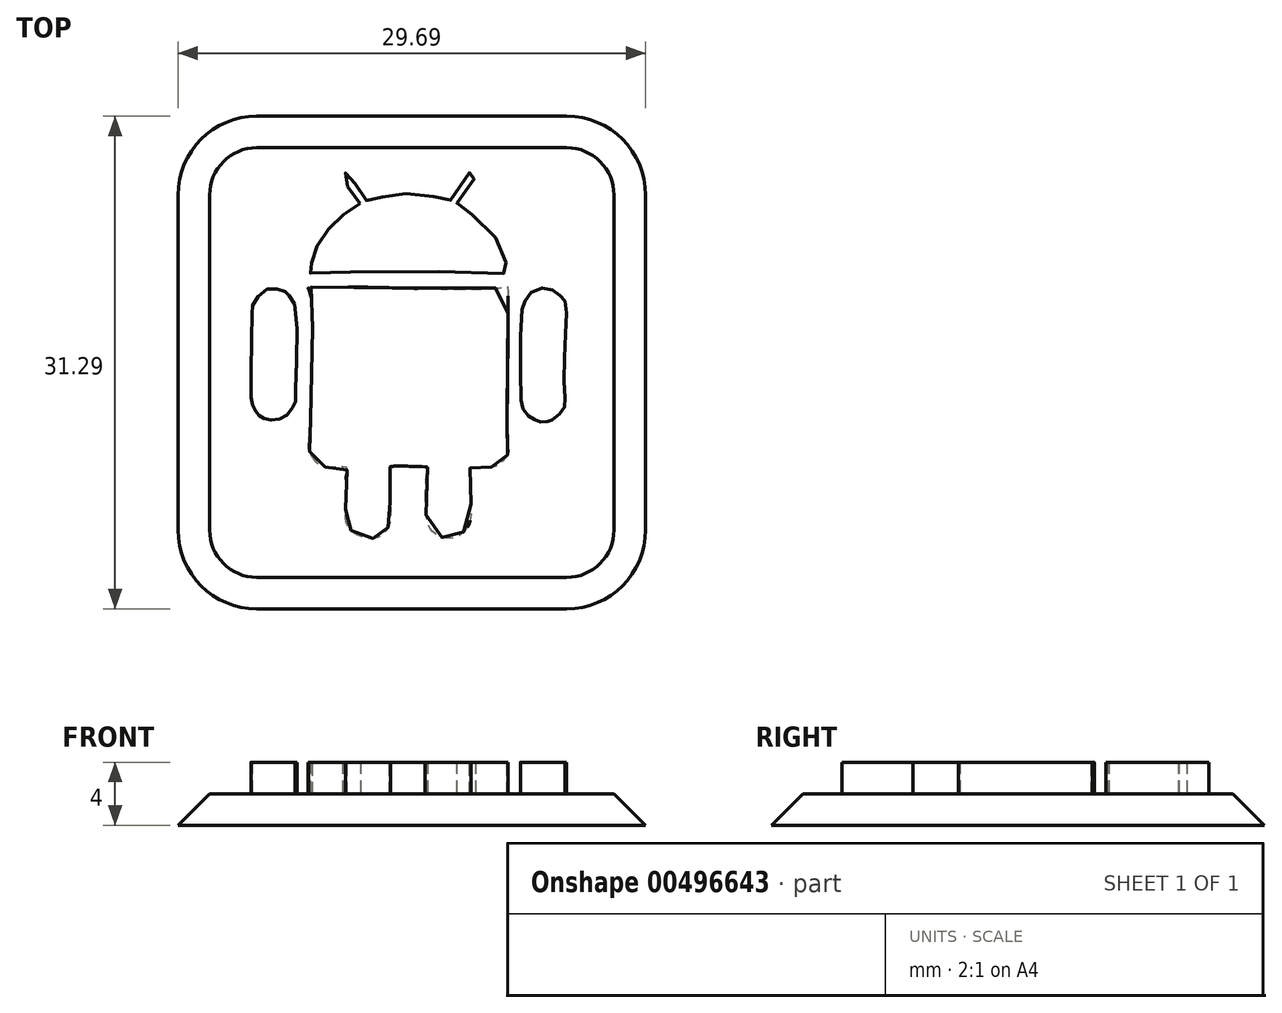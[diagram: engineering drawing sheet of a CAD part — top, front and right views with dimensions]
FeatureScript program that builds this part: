
annotation { "Feature Type Name" : "Feature", "Feature Type Description" : "" }
export const myFeature = defineFeature(function(context is Context, id is Id, definition is map)
    precondition{}
    {
        {
            var Q0;
            Q0=qCreatedBy(makeId("Top.planeOp"),FACE);
            var sketch = newSketch(context, id + "F0", { "sketchPlane" : qUnion([Q0])});
            skFitSpline(sketch, "E0", {"points": [v(6.96, 9.56) * mm, v(7.27, 9.15) * mm, v(7.6, 8.92) * mm, v(7.9, 8.8) * mm, v(8.1, 8.73) * mm, v(8.47, 8.77) * mm, v(8.65, 8.8) * mm, v(8.83, 8.9) * mm, v(9.36, 9.35) * mm, v(9.61, 9.73) * mm, v(9.59, 10.46) * mm, v(9.61, 13.76) * mm, v(9.65, 16.27) * mm, v(9.46, 16.6) * mm, v(9.1, 16.94) * mm, v(8.48, 17.25) * mm, v(7.55, 17.03) * mm, v(7.06, 16.44) * mm, v(6.88, 15.86) * mm, v(6.85, 9.87) * mm, v(6.96, 9.56) * mm]});
            skFitSpline(sketch, "E1", {"points": [v(-10.23, 9.83) * mm, v(-10.07, 9.46) * mm, v(-9.88, 9.2) * mm, v(-9.64, 9.02) * mm, v(-9.38, 8.9) * mm, v(-8.85, 8.85) * mm, v(-8.25, 9.02) * mm, v(-7.78, 9.48) * mm, v(-7.52, 10) * mm, v(-7.51, 10.18) * mm, v(-7.55, 16.14) * mm, v(-7.98, 16.83) * mm, v(-8.16, 17.03) * mm, v(-8.75, 17.2) * mm, v(-9.55, 17.05) * mm, v(-10.22, 16.15) * mm, v(-10.24, 15.87) * mm, v(-10.32, 10.12) * mm, v(-10.23, 9.83) * mm]});
            skFitSpline(sketch, "E2", {"points": [v(-3.39, 22.6) * mm, v(-4.18, 22.1) * mm, v(-5.1, 21.36) * mm, v(-5.7, 20.55) * mm, v(-6.3, 19.6) * mm, v(-6.48, 18.86) * mm, v(-6.55, 18.51) * mm, v(-6.58, 18.22) * mm, v(-6.17, 18.2) * mm, v(5.9, 18.15) * mm, v(6, 18.13) * mm, v(5.75, 19.3) * mm, v(4.78, 20.97) * mm, v(2.9, 22.45) * mm, v(2.73, 22.59) * mm, v(3.89, 24.25) * mm, v(3.89, 24.54) * mm, v(3.63, 24.64) * mm, v(2.3, 22.74) * mm, v(2.27, 22.73) * mm, v(0.73, 23.16) * mm, v(-0.9, 23.2) * mm, v(-2.35, 22.93) * mm, v(-2.93, 22.77) * mm, v(-3.16, 23.11) * mm, v(-3.97, 24.23) * mm, v(-4.23, 24.56) * mm, v(-4.43, 24.51) * mm, v(-4.51, 24.3) * mm, v(-3.48, 22.77) * mm, v(-3.39, 22.6) * mm]});
            skFitSpline(sketch, "E3", {"points": [v(-1.5, 5.85) * mm, v(-1.5, 3.85) * mm, v(-1.48, 2.52) * mm, v(-1.73, 1.87) * mm, v(-2.2, 1.44) * mm, v(-2.76, 1.34) * mm, v(-3.71, 1.63) * mm, v(-4.26, 2.33) * mm, v(-4.31, 3.04) * mm, v(-4.24, 5.64) * mm, v(-4.26, 5.87) * mm, v(-5.64, 5.87) * mm, v(-6.26, 6.27) * mm, v(-6.66, 7) * mm, v(-6.65, 7.58) * mm, v(-6.6, 16.96) * mm, v(-6.61, 17.28) * mm, v(5.71, 17.3) * mm, v(5.97, 17.3) * mm, v(5.98, 7.04) * mm, v(5.99, 6.69) * mm, v(5.56, 6.17) * mm, v(5.1, 5.9) * mm, v(3.87, 5.87) * mm, v(3.6, 5.83) * mm, v(3.57, 5.65) * mm, v(3.6, 2.58) * mm, v(3.24, 1.83) * mm, v(2.66, 1.4) * mm, v(1.6, 1.48) * mm, v(0.87, 2.4) * mm, v(0.88, 5.89) * mm], "startDerivative": vector(-1.38, -52.63) * mm, "endDerivative": vector(6.9, 77.46) * mm});
            skFitSpline(sketch, "E4", {"points": [v(0.88, 5.89) * mm, v(-1.5, 5.89) * mm, v(-1.5, 5.85) * mm], "startDerivative": vector(-3.87, 0.15) * mm, "endDerivative": vector(-0.1, -0.44) * mm});
            skLineSegment(sketch, "E5.bottom", {"start": v(-9.96, 28.16) * mm, "end": v(9.73, 28.16) * mm});
            skLineSegment(sketch, "E5.top", {"start": v(-9.96, -3.13) * mm, "end": v(9.73, -3.13) * mm});
            skLineSegment(sketch, "E5.left", {"start": v(-14.96, 23.16) * mm, "end": v(-14.96, 1.87) * mm});
            skLineSegment(sketch, "E5.right", {"start": v(14.73, 23.16) * mm, "end": v(14.73, 1.87) * mm});
            skPoint(sketch, "E6.visualSharp", {"position": v(-14.96, 28.16) * mm});
            skArc(sketch, "E6.filletArc", {"start": v(-9.96, 28.16) * mm, "mid": v(-13.5, 26.7) * mm, "end": v(-14.96, 23.16) * mm});
            skPoint(sketch, "E7.visualSharp", {"position": v(14.73, 28.16) * mm});
            skArc(sketch, "E7.filletArc", {"start": v(14.73, 23.16) * mm, "mid": v(13.26, 26.7) * mm, "end": v(9.73, 28.16) * mm});
            skPoint(sketch, "E8.visualSharp", {"position": v(14.73, -3.13) * mm});
            skArc(sketch, "E8.filletArc", {"start": v(9.73, -3.13) * mm, "mid": v(13.26, -1.67) * mm, "end": v(14.73, 1.87) * mm});
            skPoint(sketch, "E9.visualSharp", {"position": v(-14.96, -3.13) * mm});
            skArc(sketch, "E9.filletArc", {"start": v(-14.96, 1.87) * mm, "mid": v(-13.5, -1.67) * mm, "end": v(-9.96, -3.13) * mm});
            skSolve(sketch);
        }
        {
            var Q0;
            Q0 = qSketchRegion(id + "F0", true);
            extrude(context, id + "F1", {"entities" : qUnion([Q0]), "depth" : 2 * mm, "offsetDistance" : 25 * mm});
        }
        {
            var Q0;
            Q0=makeQuery(id+"F0.imprint","IMPRINT",FACE,{"disambiguationData":[TD([[makeQuery(id+"F0.imprint","IMPRINT",EDGE,{"derivedFrom":sQuery(id+"F0.wireOp",EDGE,"E2")}),1.0]])]});
            var Q1;
            Q1=makeQuery(id+"F0.imprint","IMPRINT",FACE,{"disambiguationData":[TD([[makeQuery(id+"F0.imprint","IMPRINT",EDGE,{"derivedFrom":sQuery(id+"F0.wireOp",EDGE,"E1")}),1.0]])]});
            var Q2;
            Q2=makeQuery(id+"F0.imprint","IMPRINT",FACE,{"disambiguationData":[TD([[makeQuery(id+"F0.imprint","IMPRINT",EDGE,{"derivedFrom":sQuery(id+"F0.wireOp",EDGE,"E3")}),-1.0]])]});
            var Q3;
            Q3=makeQuery(id+"F0.imprint","IMPRINT",FACE,{"disambiguationData":[TD([[makeQuery(id+"F0.imprint","IMPRINT",EDGE,{"derivedFrom":sQuery(id+"F0.wireOp",EDGE,"E0")}),1.0]])]});
            extrude(context, id + "F2", {"entities" : qUnion([Q0, Q1, Q2, Q3]), "operationType" : NewBodyOperationType.ADD, "depth" : 4 * mm, "offsetDistance" : 25 * mm});
        }
        {
            var Q0;
            Q0=makeQuery(id+"F1.opExtrude","CAP_EDGE",EDGE,{"disambiguationData":[OSD([sQuery(id+"F0.wireOp",EDGE,"E5.right")])],"isStart":false});
            chamfer(context, id + "F3", {"entities" : qUnion([Q0]), "width" : 2 * mm, "tangentPropagation" : true});
        }
    });
